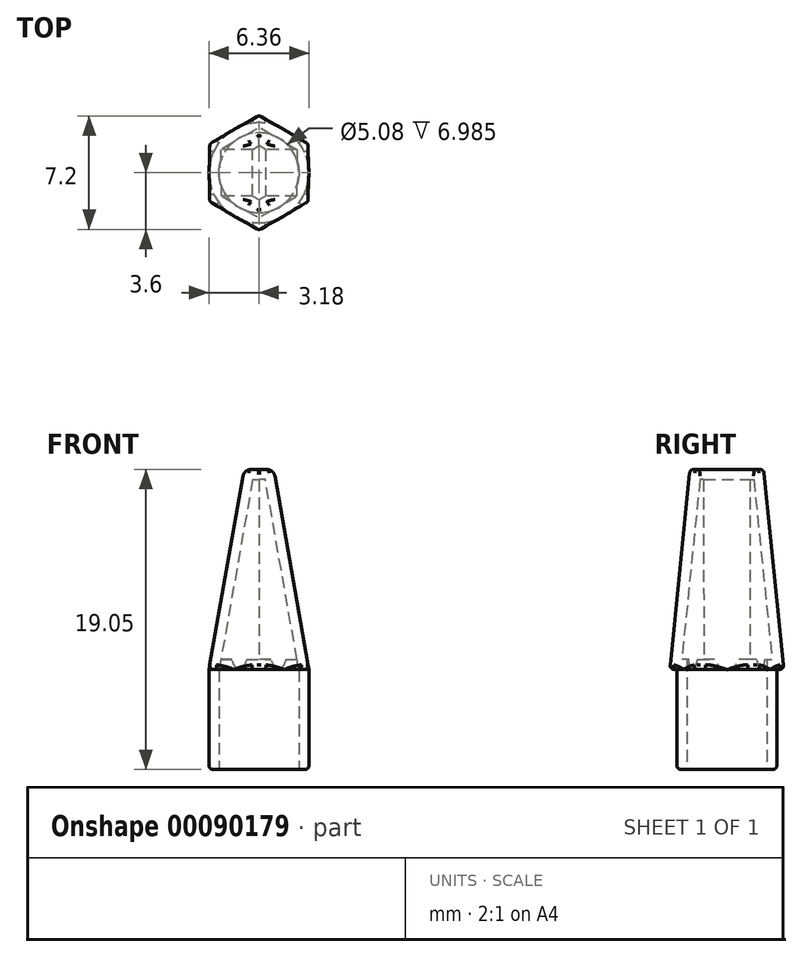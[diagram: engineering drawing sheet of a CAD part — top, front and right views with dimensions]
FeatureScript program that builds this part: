
annotation { "Feature Type Name" : "Feature", "Feature Type Description" : "" }
export const myFeature = defineFeature(function(context is Context, id is Id, definition is map)
    precondition{}
    {
        {
            var Q0;
            Q0=qCreatedBy(makeId("Top.planeOp"),FACE);
            var sketch = newSketch(context, id + "F0", { "sketchPlane" : qUnion([Q0])});
            skCircle(sketch, "E0", {"center": v(0, 0) * mm, "radius": 3.18 * mm});
            skSolve(sketch);
        }
        {
            var Q0;
            Q0=makeQuery(id+"F0.imprint","IMPRINT",FACE,{"disambiguationData":[TD([[makeQuery(id+"F0.imprint","IMPRINT",EDGE,{"derivedFrom":sQuery(id+"F0.wireOp",EDGE,"E0")}),1.0]])]});
            extrude(context, id + "F1", {"entities" : qUnion([Q0]), "depth" : 6.35 * mm});
        }
        {
            var Q0;
            Q0=makeQuery(id+"F1.opExtrude","CAP_FACE",FACE,{"disambiguationData":[OSD([sQuery(id+"F0.wireOp",EDGE,"E0")])],"isStart":false});
            var sketch = newSketch(context, id + "F2", { "sketchPlane" : qUnion([Q0])});
            skCircle(sketch, "E1.cCircle", {"center": v(0, 0) * mm, "radius": 3.18 * mm, "construction": true});
            skLineSegment(sketch, "E1.0", {"start": v(-3.18, -1.83) * mm, "end": v(-3.18, 1.83) * mm});
            skLineSegment(sketch, "E1.1", {"start": v(-3.17, 1.83) * mm, "end": v(0, 3.67) * mm});
            skLineSegment(sketch, "E1.2", {"start": v(0, 3.67) * mm, "end": v(3.17, 1.83) * mm});
            skLineSegment(sketch, "E1.3", {"start": v(3.17, 1.83) * mm, "end": v(3.18, -1.83) * mm});
            skLineSegment(sketch, "E1.4", {"start": v(3.18, -1.83) * mm, "end": v(0, -3.67) * mm});
            skLineSegment(sketch, "E1.5", {"start": v(0, -3.67) * mm, "end": v(-3.17, -1.83) * mm});
            skPoint(sketch, "E1.0.midPoint", {"position": v(-3.18, 0) * mm});
            skSolve(sketch);
        }
        {
            var Q0;
            {var subQ0=sQuery(id+"F2.wireOp",EDGE,"E1.5");var subQ1=sQuery(id+"F2.wireOp",EDGE,"E1.0");var subQ2=makeQuery(id+"F2.imprint","INTERSECT",VERTEX,{"derivedFrom":[subQ1,subQ0]});Q0=makeQuery(id+"F2.imprint","IMPRINT",FACE,{"disambiguationData":[TD([[makeQuery(id+"F2.imprint","IMPRINT",EDGE,{"disambiguationData":[TD([[subQ2,-1.0]])],"derivedFrom":subQ1}),-1.0]])]});}
            var Q1;
            {var subQ0=sQuery(id+"F2.wireOp",EDGE,"E1.2");var subQ1=sQuery(id+"F2.wireOp",EDGE,"E1.1");var subQ2=makeQuery(id+"F2.imprint","INTERSECT",VERTEX,{"derivedFrom":[subQ1,subQ0]});Q1=makeQuery(id+"F2.imprint","IMPRINT",FACE,{"disambiguationData":[TD([[makeQuery(id+"F2.imprint","IMPRINT",EDGE,{"disambiguationData":[TD([[subQ2,1.0]])],"derivedFrom":subQ1}),-1.0]])]});}
            var Q2;
            {var subQ0=sQuery(id+"F2.wireOp",EDGE,"E1.3");var subQ1=sQuery(id+"F2.wireOp",EDGE,"E1.2");var subQ2=makeQuery(id+"F2.imprint","INTERSECT",VERTEX,{"derivedFrom":[subQ1,subQ0]});Q2=makeQuery(id+"F2.imprint","IMPRINT",FACE,{"disambiguationData":[TD([[makeQuery(id+"F2.imprint","IMPRINT",EDGE,{"disambiguationData":[TD([[subQ2,1.0]])],"derivedFrom":subQ1}),-1.0]])]});}
            var Q3;
            {var subQ0=sQuery(id+"F2.wireOp",EDGE,"E1.4");var subQ1=sQuery(id+"F2.wireOp",EDGE,"E1.3");var subQ2=makeQuery(id+"F2.imprint","INTERSECT",VERTEX,{"derivedFrom":[subQ1,subQ0]});Q3=makeQuery(id+"F2.imprint","IMPRINT",FACE,{"disambiguationData":[TD([[makeQuery(id+"F2.imprint","IMPRINT",EDGE,{"disambiguationData":[TD([[subQ2,1.0]])],"derivedFrom":subQ1}),-1.0]])]});}
            var Q4;
            {var subQ0=sQuery(id+"F2.wireOp",EDGE,"E1.5");var subQ1=sQuery(id+"F2.wireOp",EDGE,"E1.4");var subQ2=makeQuery(id+"F2.imprint","INTERSECT",VERTEX,{"derivedFrom":[subQ1,subQ0]});Q4=makeQuery(id+"F2.imprint","IMPRINT",FACE,{"disambiguationData":[TD([[makeQuery(id+"F2.imprint","IMPRINT",EDGE,{"disambiguationData":[TD([[subQ2,1.0]])],"derivedFrom":subQ1}),-1.0]])]});}
            var Q5;
            {var subQ0=makeQuery(id+"F1.opExtrude","CAP_EDGE",EDGE,{"disambiguationData":[OSD([sQuery(id+"F0.wireOp",EDGE,"E0")])],"isStart":false});var subQ6=makeQuery(id+"F2.imprint","INTERSECT",VERTEX,{"derivedFrom":[subQ0,sQuery(id+"F2.wireOp",EDGE,"E1.0")]});Q5=makeQuery(id+"F2.imprint","IMPRINT",FACE,{"disambiguationData":[TD([[makeQuery(id+"F2.imprint","IMPRINT",EDGE,{"disambiguationData":[TD([[subQ6,1.0]])],"derivedFrom":subQ0}),1.0]])]});}
            var Q6;
            {var subQ0=sQuery(id+"F2.wireOp",EDGE,"E1.1");var subQ1=sQuery(id+"F2.wireOp",EDGE,"E1.0");var subQ2=makeQuery(id+"F2.imprint","INTERSECT",VERTEX,{"derivedFrom":[subQ1,subQ0]});Q6=makeQuery(id+"F2.imprint","IMPRINT",FACE,{"disambiguationData":[TD([[makeQuery(id+"F2.imprint","IMPRINT",EDGE,{"disambiguationData":[TD([[subQ2,1.0]])],"derivedFrom":subQ1}),-1.0]])]});}
            extrude(context, id + "F3", {"entities" : qUnion([Q0, Q1, Q2, Q3, Q4, Q5, Q6]), "operationType" : NewBodyOperationType.ADD, "depth" : 12.7 * mm});
        }
        {
            var Q0;
            Q0=makeQuery(id+"F3.opExtrude","CAP_EDGE",EDGE,{"disambiguationData":[OSD([sQuery(id+"F2.wireOp",EDGE,"E1.3")])],"isStart":false});
            var Q1;
            Q1=makeQuery(id+"F3.opExtrude","CAP_EDGE",EDGE,{"disambiguationData":[OSD([sQuery(id+"F2.wireOp",EDGE,"E1.0")])],"isStart":false});
            chamfer(context, id + "F4", {"entities" : qUnion([Q0, Q1]), "chamferType" : ChamferType.OFFSET_ANGLE, "width" : 12.7 * mm, "oppositeDirection" : false, "angle" : 10 * degree, "tangentPropagation" : true});
        }
        {
            var Q0;
            Q0=makeQuery(id+"F3.opExtrude","CAP_EDGE",EDGE,{"disambiguationData":[OSD([sQuery(id+"F2.wireOp",EDGE,"E1.2")])],"isStart":false});
            var Q1;
            Q1=makeQuery(id+"F3.opExtrude","CAP_EDGE",EDGE,{"disambiguationData":[OSD([sQuery(id+"F2.wireOp",EDGE,"E1.1")])],"isStart":false});
            var Q2;
            Q2=makeQuery(id+"F3.opExtrude","CAP_EDGE",EDGE,{"disambiguationData":[OSD([sQuery(id+"F2.wireOp",EDGE,"E1.4")])],"isStart":false});
            var Q3;
            Q3=makeQuery(id+"F3.opExtrude","CAP_EDGE",EDGE,{"disambiguationData":[OSD([sQuery(id+"F2.wireOp",EDGE,"E1.5")])],"isStart":false});
            chamfer(context, id + "F5", {"entities" : qUnion([Q0, Q1, Q2, Q3]), "chamferType" : ChamferType.OFFSET_ANGLE, "width" : 12.7 * mm, "oppositeDirection" : false, "angle" : 5 * degree, "tangentPropagation" : true});
        }
        {
            var Q0;
            {var subQ0=sQuery(id+"F2.wireOp",EDGE,"E1.2");Q0=makeQuery(id+"F5.opChamfer","BLEND_EDGE",EDGE,{"blendedFrom":[makeQuery(id+"F3.opExtrude","CAP_EDGE",EDGE,{"disambiguationData":[OSD([subQ0])],"isStart":false}),makeQuery(id+"F3.opExtrude","CAP_FACE",FACE,{"disambiguationData":[OSD([sQuery(id+"F2.wireOp",EDGE,"E1.0"),sQuery(id+"F2.wireOp",EDGE,"E1.1"),subQ0,sQuery(id+"F2.wireOp",EDGE,"E1.3"),sQuery(id+"F2.wireOp",EDGE,"E1.4"),sQuery(id+"F2.wireOp",EDGE,"E1.5")])],"isStart":false})],"blendedInto":[makeQuery(id+"F3.opExtrude","CAP_FACE",FACE,{"disambiguationData":[OSD([sQuery(id+"F2.wireOp",EDGE,"E1.0"),sQuery(id+"F2.wireOp",EDGE,"E1.1"),subQ0,sQuery(id+"F2.wireOp",EDGE,"E1.3"),sQuery(id+"F2.wireOp",EDGE,"E1.4"),sQuery(id+"F2.wireOp",EDGE,"E1.5")])],"isStart":false})]});}
            var Q1;
            {var subQ0=sQuery(id+"F2.wireOp",EDGE,"E1.1");Q1=makeQuery(id+"F5.opChamfer","BLEND_EDGE",EDGE,{"blendedFrom":[makeQuery(id+"F3.opExtrude","CAP_EDGE",EDGE,{"disambiguationData":[OSD([subQ0])],"isStart":false}),makeQuery(id+"F3.opExtrude","CAP_FACE",FACE,{"disambiguationData":[OSD([sQuery(id+"F2.wireOp",EDGE,"E1.0"),subQ0,sQuery(id+"F2.wireOp",EDGE,"E1.2"),sQuery(id+"F2.wireOp",EDGE,"E1.3"),sQuery(id+"F2.wireOp",EDGE,"E1.4"),sQuery(id+"F2.wireOp",EDGE,"E1.5")])],"isStart":false})],"blendedInto":[makeQuery(id+"F3.opExtrude","CAP_FACE",FACE,{"disambiguationData":[OSD([sQuery(id+"F2.wireOp",EDGE,"E1.0"),subQ0,sQuery(id+"F2.wireOp",EDGE,"E1.2"),sQuery(id+"F2.wireOp",EDGE,"E1.3"),sQuery(id+"F2.wireOp",EDGE,"E1.4"),sQuery(id+"F2.wireOp",EDGE,"E1.5")])],"isStart":false})]});}
            var Q2;
            {var subQ0=sQuery(id+"F2.wireOp",EDGE,"E1.5");Q2=makeQuery(id+"F5.opChamfer","BLEND_EDGE",EDGE,{"blendedFrom":[makeQuery(id+"F3.opExtrude","CAP_EDGE",EDGE,{"disambiguationData":[OSD([subQ0])],"isStart":false}),makeQuery(id+"F3.opExtrude","CAP_FACE",FACE,{"disambiguationData":[OSD([sQuery(id+"F2.wireOp",EDGE,"E1.0"),sQuery(id+"F2.wireOp",EDGE,"E1.1"),sQuery(id+"F2.wireOp",EDGE,"E1.2"),sQuery(id+"F2.wireOp",EDGE,"E1.3"),sQuery(id+"F2.wireOp",EDGE,"E1.4"),subQ0])],"isStart":false})],"blendedInto":[makeQuery(id+"F3.opExtrude","CAP_FACE",FACE,{"disambiguationData":[OSD([sQuery(id+"F2.wireOp",EDGE,"E1.0"),sQuery(id+"F2.wireOp",EDGE,"E1.1"),sQuery(id+"F2.wireOp",EDGE,"E1.2"),sQuery(id+"F2.wireOp",EDGE,"E1.3"),sQuery(id+"F2.wireOp",EDGE,"E1.4"),subQ0])],"isStart":false})]});}
            var Q3;
            {var subQ0=sQuery(id+"F2.wireOp",EDGE,"E1.4");Q3=makeQuery(id+"F5.opChamfer","BLEND_EDGE",EDGE,{"blendedFrom":[makeQuery(id+"F3.opExtrude","CAP_EDGE",EDGE,{"disambiguationData":[OSD([subQ0])],"isStart":false}),makeQuery(id+"F3.opExtrude","CAP_FACE",FACE,{"disambiguationData":[OSD([sQuery(id+"F2.wireOp",EDGE,"E1.0"),sQuery(id+"F2.wireOp",EDGE,"E1.1"),sQuery(id+"F2.wireOp",EDGE,"E1.2"),sQuery(id+"F2.wireOp",EDGE,"E1.3"),subQ0,sQuery(id+"F2.wireOp",EDGE,"E1.5")])],"isStart":false})],"blendedInto":[makeQuery(id+"F3.opExtrude","CAP_FACE",FACE,{"disambiguationData":[OSD([sQuery(id+"F2.wireOp",EDGE,"E1.0"),sQuery(id+"F2.wireOp",EDGE,"E1.1"),sQuery(id+"F2.wireOp",EDGE,"E1.2"),sQuery(id+"F2.wireOp",EDGE,"E1.3"),subQ0,sQuery(id+"F2.wireOp",EDGE,"E1.5")])],"isStart":false})]});}
            var Q4;
            Q4=makeQuery(id+"F5.opChamfer","BLEND_EDGE",EDGE,{"blendedFrom":[makeQuery(id+"F3.opExtrude","CAP_EDGE",EDGE,{"disambiguationData":[OSD([sQuery(id+"F2.wireOp",EDGE,"E1.2")])],"isStart":false}),makeQuery(id+"F4.opChamfer","BLEND_FACE",FACE,{"disambiguationData":[OSD([sQuery(id+"F2.wireOp",EDGE,"E1.3")])]})],"blendedInto":[makeQuery(id+"F4.opChamfer","BLEND_FACE",FACE,{"disambiguationData":[OSD([sQuery(id+"F2.wireOp",EDGE,"E1.3")])]})]});
            var Q5;
            Q5=makeQuery(id+"F5.opChamfer","BLEND_EDGE",EDGE,{"blendedFrom":[makeQuery(id+"F3.opExtrude","CAP_EDGE",EDGE,{"disambiguationData":[OSD([sQuery(id+"F2.wireOp",EDGE,"E1.1")])],"isStart":false}),makeQuery(id+"F3.opExtrude","CAP_EDGE",EDGE,{"disambiguationData":[OSD([sQuery(id+"F2.wireOp",EDGE,"E1.2")])],"isStart":false})],"blendedInto":[]});
            var Q6;
            Q6=makeQuery(id+"F5.opChamfer","BLEND_EDGE",EDGE,{"blendedFrom":[makeQuery(id+"F3.opExtrude","CAP_EDGE",EDGE,{"disambiguationData":[OSD([sQuery(id+"F2.wireOp",EDGE,"E1.1")])],"isStart":false}),makeQuery(id+"F4.opChamfer","BLEND_FACE",FACE,{"disambiguationData":[OSD([sQuery(id+"F2.wireOp",EDGE,"E1.0")])]})],"blendedInto":[makeQuery(id+"F4.opChamfer","BLEND_FACE",FACE,{"disambiguationData":[OSD([sQuery(id+"F2.wireOp",EDGE,"E1.0")])]})]});
            var Q7;
            Q7=makeQuery(id+"F5.opChamfer","BLEND_EDGE",EDGE,{"blendedFrom":[makeQuery(id+"F3.opExtrude","CAP_EDGE",EDGE,{"disambiguationData":[OSD([sQuery(id+"F2.wireOp",EDGE,"E1.5")])],"isStart":false}),makeQuery(id+"F4.opChamfer","BLEND_FACE",FACE,{"disambiguationData":[OSD([sQuery(id+"F2.wireOp",EDGE,"E1.0")])]})],"blendedInto":[makeQuery(id+"F4.opChamfer","BLEND_FACE",FACE,{"disambiguationData":[OSD([sQuery(id+"F2.wireOp",EDGE,"E1.0")])]})]});
            var Q8;
            Q8=makeQuery(id+"F5.opChamfer","BLEND_EDGE",EDGE,{"blendedFrom":[makeQuery(id+"F3.opExtrude","CAP_EDGE",EDGE,{"disambiguationData":[OSD([sQuery(id+"F2.wireOp",EDGE,"E1.4")])],"isStart":false}),makeQuery(id+"F3.opExtrude","CAP_EDGE",EDGE,{"disambiguationData":[OSD([sQuery(id+"F2.wireOp",EDGE,"E1.5")])],"isStart":false})],"blendedInto":[]});
            var Q9;
            Q9=makeQuery(id+"F5.opChamfer","BLEND_EDGE",EDGE,{"blendedFrom":[makeQuery(id+"F3.opExtrude","CAP_EDGE",EDGE,{"disambiguationData":[OSD([sQuery(id+"F2.wireOp",EDGE,"E1.4")])],"isStart":false}),makeQuery(id+"F4.opChamfer","BLEND_FACE",FACE,{"disambiguationData":[OSD([sQuery(id+"F2.wireOp",EDGE,"E1.3")])]})],"blendedInto":[makeQuery(id+"F4.opChamfer","BLEND_FACE",FACE,{"disambiguationData":[OSD([sQuery(id+"F2.wireOp",EDGE,"E1.3")])]})]});
            var Q10;
            {var subQ0=sQuery(id+"F2.wireOp",EDGE,"E1.5");var subQ1=sQuery(id+"F2.wireOp",EDGE,"E1.4");var subQ2=makeQuery(id+"F3.opExtrude","CAP_FACE",FACE,{"disambiguationData":[OSD([sQuery(id+"F2.wireOp",EDGE,"E1.0"),sQuery(id+"F2.wireOp",EDGE,"E1.1"),sQuery(id+"F2.wireOp",EDGE,"E1.2"),sQuery(id+"F2.wireOp",EDGE,"E1.3"),subQ1,subQ0])],"isStart":true});Q10=makeQuery(id+"F5.opChamfer","BLEND_EDGE",EDGE,{"blendedFrom":[makeQuery(id+"F3.opExtrude","CAP_EDGE",EDGE,{"disambiguationData":[OSD([subQ0])],"isStart":false}),makeQuery(id+"F3.boolean.opBoolean","SPLIT",FACE,{"disambiguationData":[TD([makeQuery(id+"F1.opExtrude","SWEPT_FACE",FACE,{"disambiguationData":[OSD([sQuery(id+"F0.wireOp",EDGE,"E0")])]}),subQ2,makeQuery(id+"F3.opExtrude","SWEPT_FACE",FACE,{"disambiguationData":[OSD([subQ1])]}),makeQuery(id+"F3.opExtrude","SWEPT_FACE",FACE,{"disambiguationData":[OSD([subQ0])]})])],"derivedFrom":subQ2})],"blendedInto":[makeQuery(id+"F3.boolean.opBoolean","SPLIT",FACE,{"disambiguationData":[TD([makeQuery(id+"F1.opExtrude","SWEPT_FACE",FACE,{"disambiguationData":[OSD([sQuery(id+"F0.wireOp",EDGE,"E0")])]}),subQ2,makeQuery(id+"F3.opExtrude","SWEPT_FACE",FACE,{"disambiguationData":[OSD([subQ1])]}),makeQuery(id+"F3.opExtrude","SWEPT_FACE",FACE,{"disambiguationData":[OSD([subQ0])]})])],"derivedFrom":subQ2})]});}
            var Q11;
            {var subQ0=sQuery(id+"F2.wireOp",EDGE,"E1.0");var subQ1=sQuery(id+"F2.wireOp",EDGE,"E1.5");var subQ2=makeQuery(id+"F3.opExtrude","CAP_FACE",FACE,{"disambiguationData":[OSD([subQ0,sQuery(id+"F2.wireOp",EDGE,"E1.1"),sQuery(id+"F2.wireOp",EDGE,"E1.2"),sQuery(id+"F2.wireOp",EDGE,"E1.3"),sQuery(id+"F2.wireOp",EDGE,"E1.4"),subQ1])],"isStart":true});Q11=makeQuery(id+"F5.opChamfer","BLEND_EDGE",EDGE,{"blendedFrom":[makeQuery(id+"F3.opExtrude","CAP_EDGE",EDGE,{"disambiguationData":[OSD([subQ1])],"isStart":false}),makeQuery(id+"F3.boolean.opBoolean","SPLIT",FACE,{"disambiguationData":[TD([makeQuery(id+"F1.opExtrude","SWEPT_FACE",FACE,{"disambiguationData":[OSD([sQuery(id+"F0.wireOp",EDGE,"E0")])]}),makeQuery(id+"F3.opExtrude","SWEPT_FACE",FACE,{"disambiguationData":[OSD([subQ0])]}),subQ2,makeQuery(id+"F3.opExtrude","SWEPT_FACE",FACE,{"disambiguationData":[OSD([subQ1])]})])],"derivedFrom":subQ2})],"blendedInto":[makeQuery(id+"F3.boolean.opBoolean","SPLIT",FACE,{"disambiguationData":[TD([makeQuery(id+"F1.opExtrude","SWEPT_FACE",FACE,{"disambiguationData":[OSD([sQuery(id+"F0.wireOp",EDGE,"E0")])]}),makeQuery(id+"F3.opExtrude","SWEPT_FACE",FACE,{"disambiguationData":[OSD([subQ0])]}),subQ2,makeQuery(id+"F3.opExtrude","SWEPT_FACE",FACE,{"disambiguationData":[OSD([subQ1])]})])],"derivedFrom":subQ2})]});}
            var Q12;
            {var subQ0=sQuery(id+"F2.wireOp",EDGE,"E1.5");var subQ1=sQuery(id+"F2.wireOp",EDGE,"E1.4");var subQ2=makeQuery(id+"F3.opExtrude","CAP_FACE",FACE,{"disambiguationData":[OSD([sQuery(id+"F2.wireOp",EDGE,"E1.0"),sQuery(id+"F2.wireOp",EDGE,"E1.1"),sQuery(id+"F2.wireOp",EDGE,"E1.2"),sQuery(id+"F2.wireOp",EDGE,"E1.3"),subQ1,subQ0])],"isStart":true});Q12=makeQuery(id+"F5.opChamfer","BLEND_EDGE",EDGE,{"blendedFrom":[makeQuery(id+"F3.opExtrude","CAP_EDGE",EDGE,{"disambiguationData":[OSD([subQ1])],"isStart":false}),makeQuery(id+"F3.boolean.opBoolean","SPLIT",FACE,{"disambiguationData":[TD([makeQuery(id+"F1.opExtrude","SWEPT_FACE",FACE,{"disambiguationData":[OSD([sQuery(id+"F0.wireOp",EDGE,"E0")])]}),subQ2,makeQuery(id+"F3.opExtrude","SWEPT_FACE",FACE,{"disambiguationData":[OSD([subQ1])]}),makeQuery(id+"F3.opExtrude","SWEPT_FACE",FACE,{"disambiguationData":[OSD([subQ0])]})])],"derivedFrom":subQ2})],"blendedInto":[makeQuery(id+"F3.boolean.opBoolean","SPLIT",FACE,{"disambiguationData":[TD([makeQuery(id+"F1.opExtrude","SWEPT_FACE",FACE,{"disambiguationData":[OSD([sQuery(id+"F0.wireOp",EDGE,"E0")])]}),subQ2,makeQuery(id+"F3.opExtrude","SWEPT_FACE",FACE,{"disambiguationData":[OSD([subQ1])]}),makeQuery(id+"F3.opExtrude","SWEPT_FACE",FACE,{"disambiguationData":[OSD([subQ0])]})])],"derivedFrom":subQ2})]});}
            var Q13;
            {var subQ0=sQuery(id+"F2.wireOp",EDGE,"E1.4");var subQ1=sQuery(id+"F2.wireOp",EDGE,"E1.3");var subQ2=makeQuery(id+"F3.opExtrude","CAP_FACE",FACE,{"disambiguationData":[OSD([sQuery(id+"F2.wireOp",EDGE,"E1.0"),sQuery(id+"F2.wireOp",EDGE,"E1.1"),sQuery(id+"F2.wireOp",EDGE,"E1.2"),subQ1,subQ0,sQuery(id+"F2.wireOp",EDGE,"E1.5")])],"isStart":true});Q13=makeQuery(id+"F5.opChamfer","BLEND_EDGE",EDGE,{"blendedFrom":[makeQuery(id+"F3.opExtrude","CAP_EDGE",EDGE,{"disambiguationData":[OSD([subQ0])],"isStart":false}),makeQuery(id+"F3.boolean.opBoolean","SPLIT",FACE,{"disambiguationData":[TD([makeQuery(id+"F1.opExtrude","SWEPT_FACE",FACE,{"disambiguationData":[OSD([sQuery(id+"F0.wireOp",EDGE,"E0")])]}),subQ2,makeQuery(id+"F3.opExtrude","SWEPT_FACE",FACE,{"disambiguationData":[OSD([subQ1])]}),makeQuery(id+"F3.opExtrude","SWEPT_FACE",FACE,{"disambiguationData":[OSD([subQ0])]})])],"derivedFrom":subQ2})],"blendedInto":[makeQuery(id+"F3.boolean.opBoolean","SPLIT",FACE,{"disambiguationData":[TD([makeQuery(id+"F1.opExtrude","SWEPT_FACE",FACE,{"disambiguationData":[OSD([sQuery(id+"F0.wireOp",EDGE,"E0")])]}),subQ2,makeQuery(id+"F3.opExtrude","SWEPT_FACE",FACE,{"disambiguationData":[OSD([subQ1])]}),makeQuery(id+"F3.opExtrude","SWEPT_FACE",FACE,{"disambiguationData":[OSD([subQ0])]})])],"derivedFrom":subQ2})]});}
            var Q14;
            {var subQ0=sQuery(id+"F2.wireOp",EDGE,"E1.0");var subQ1=sQuery(id+"F2.wireOp",EDGE,"E1.1");var subQ2=makeQuery(id+"F3.opExtrude","CAP_FACE",FACE,{"disambiguationData":[OSD([subQ0,subQ1,sQuery(id+"F2.wireOp",EDGE,"E1.2"),sQuery(id+"F2.wireOp",EDGE,"E1.3"),sQuery(id+"F2.wireOp",EDGE,"E1.4"),sQuery(id+"F2.wireOp",EDGE,"E1.5")])],"isStart":true});Q14=makeQuery(id+"F4.opChamfer","BLEND_EDGE",EDGE,{"blendedFrom":[makeQuery(id+"F3.opExtrude","CAP_EDGE",EDGE,{"disambiguationData":[OSD([subQ0])],"isStart":false}),makeQuery(id+"F3.boolean.opBoolean","SPLIT",FACE,{"disambiguationData":[TD([makeQuery(id+"F1.opExtrude","SWEPT_FACE",FACE,{"disambiguationData":[OSD([sQuery(id+"F0.wireOp",EDGE,"E0")])]}),makeQuery(id+"F3.opExtrude","SWEPT_FACE",FACE,{"disambiguationData":[OSD([subQ0])]}),subQ2,makeQuery(id+"F3.opExtrude","SWEPT_FACE",FACE,{"disambiguationData":[OSD([subQ1])]})])],"derivedFrom":subQ2})],"blendedInto":[makeQuery(id+"F3.boolean.opBoolean","SPLIT",FACE,{"disambiguationData":[TD([makeQuery(id+"F1.opExtrude","SWEPT_FACE",FACE,{"disambiguationData":[OSD([sQuery(id+"F0.wireOp",EDGE,"E0")])]}),makeQuery(id+"F3.opExtrude","SWEPT_FACE",FACE,{"disambiguationData":[OSD([subQ0])]}),subQ2,makeQuery(id+"F3.opExtrude","SWEPT_FACE",FACE,{"disambiguationData":[OSD([subQ1])]})])],"derivedFrom":subQ2})]});}
            var Q15;
            {var subQ0=sQuery(id+"F2.wireOp",EDGE,"E1.0");var subQ1=sQuery(id+"F2.wireOp",EDGE,"E1.1");var subQ2=makeQuery(id+"F3.opExtrude","CAP_FACE",FACE,{"disambiguationData":[OSD([subQ0,subQ1,sQuery(id+"F2.wireOp",EDGE,"E1.2"),sQuery(id+"F2.wireOp",EDGE,"E1.3"),sQuery(id+"F2.wireOp",EDGE,"E1.4"),sQuery(id+"F2.wireOp",EDGE,"E1.5")])],"isStart":true});Q15=makeQuery(id+"F5.opChamfer","BLEND_EDGE",EDGE,{"blendedFrom":[makeQuery(id+"F3.opExtrude","CAP_EDGE",EDGE,{"disambiguationData":[OSD([subQ1])],"isStart":false}),makeQuery(id+"F3.boolean.opBoolean","SPLIT",FACE,{"disambiguationData":[TD([makeQuery(id+"F1.opExtrude","SWEPT_FACE",FACE,{"disambiguationData":[OSD([sQuery(id+"F0.wireOp",EDGE,"E0")])]}),makeQuery(id+"F3.opExtrude","SWEPT_FACE",FACE,{"disambiguationData":[OSD([subQ0])]}),subQ2,makeQuery(id+"F3.opExtrude","SWEPT_FACE",FACE,{"disambiguationData":[OSD([subQ1])]})])],"derivedFrom":subQ2})],"blendedInto":[makeQuery(id+"F3.boolean.opBoolean","SPLIT",FACE,{"disambiguationData":[TD([makeQuery(id+"F1.opExtrude","SWEPT_FACE",FACE,{"disambiguationData":[OSD([sQuery(id+"F0.wireOp",EDGE,"E0")])]}),makeQuery(id+"F3.opExtrude","SWEPT_FACE",FACE,{"disambiguationData":[OSD([subQ0])]}),subQ2,makeQuery(id+"F3.opExtrude","SWEPT_FACE",FACE,{"disambiguationData":[OSD([subQ1])]})])],"derivedFrom":subQ2})]});}
            var Q16;
            {var subQ0=sQuery(id+"F2.wireOp",EDGE,"E1.2");var subQ1=sQuery(id+"F2.wireOp",EDGE,"E1.1");var subQ2=makeQuery(id+"F3.opExtrude","CAP_FACE",FACE,{"disambiguationData":[OSD([sQuery(id+"F2.wireOp",EDGE,"E1.0"),subQ1,subQ0,sQuery(id+"F2.wireOp",EDGE,"E1.3"),sQuery(id+"F2.wireOp",EDGE,"E1.4"),sQuery(id+"F2.wireOp",EDGE,"E1.5")])],"isStart":true});Q16=makeQuery(id+"F5.opChamfer","BLEND_EDGE",EDGE,{"blendedFrom":[makeQuery(id+"F3.opExtrude","CAP_EDGE",EDGE,{"disambiguationData":[OSD([subQ1])],"isStart":false}),makeQuery(id+"F3.boolean.opBoolean","SPLIT",FACE,{"disambiguationData":[TD([makeQuery(id+"F1.opExtrude","SWEPT_FACE",FACE,{"disambiguationData":[OSD([sQuery(id+"F0.wireOp",EDGE,"E0")])]}),subQ2,makeQuery(id+"F3.opExtrude","SWEPT_FACE",FACE,{"disambiguationData":[OSD([subQ1])]}),makeQuery(id+"F3.opExtrude","SWEPT_FACE",FACE,{"disambiguationData":[OSD([subQ0])]})])],"derivedFrom":subQ2})],"blendedInto":[makeQuery(id+"F3.boolean.opBoolean","SPLIT",FACE,{"disambiguationData":[TD([makeQuery(id+"F1.opExtrude","SWEPT_FACE",FACE,{"disambiguationData":[OSD([sQuery(id+"F0.wireOp",EDGE,"E0")])]}),subQ2,makeQuery(id+"F3.opExtrude","SWEPT_FACE",FACE,{"disambiguationData":[OSD([subQ1])]}),makeQuery(id+"F3.opExtrude","SWEPT_FACE",FACE,{"disambiguationData":[OSD([subQ0])]})])],"derivedFrom":subQ2})]});}
            var Q17;
            {var subQ0=sQuery(id+"F2.wireOp",EDGE,"E1.2");var subQ1=sQuery(id+"F2.wireOp",EDGE,"E1.1");var subQ2=makeQuery(id+"F3.opExtrude","CAP_FACE",FACE,{"disambiguationData":[OSD([sQuery(id+"F2.wireOp",EDGE,"E1.0"),subQ1,subQ0,sQuery(id+"F2.wireOp",EDGE,"E1.3"),sQuery(id+"F2.wireOp",EDGE,"E1.4"),sQuery(id+"F2.wireOp",EDGE,"E1.5")])],"isStart":true});Q17=makeQuery(id+"F5.opChamfer","BLEND_EDGE",EDGE,{"blendedFrom":[makeQuery(id+"F3.opExtrude","CAP_EDGE",EDGE,{"disambiguationData":[OSD([subQ0])],"isStart":false}),makeQuery(id+"F3.boolean.opBoolean","SPLIT",FACE,{"disambiguationData":[TD([makeQuery(id+"F1.opExtrude","SWEPT_FACE",FACE,{"disambiguationData":[OSD([sQuery(id+"F0.wireOp",EDGE,"E0")])]}),subQ2,makeQuery(id+"F3.opExtrude","SWEPT_FACE",FACE,{"disambiguationData":[OSD([subQ1])]}),makeQuery(id+"F3.opExtrude","SWEPT_FACE",FACE,{"disambiguationData":[OSD([subQ0])]})])],"derivedFrom":subQ2})],"blendedInto":[makeQuery(id+"F3.boolean.opBoolean","SPLIT",FACE,{"disambiguationData":[TD([makeQuery(id+"F1.opExtrude","SWEPT_FACE",FACE,{"disambiguationData":[OSD([sQuery(id+"F0.wireOp",EDGE,"E0")])]}),subQ2,makeQuery(id+"F3.opExtrude","SWEPT_FACE",FACE,{"disambiguationData":[OSD([subQ1])]}),makeQuery(id+"F3.opExtrude","SWEPT_FACE",FACE,{"disambiguationData":[OSD([subQ0])]})])],"derivedFrom":subQ2})]});}
            var Q18;
            {var subQ0=sQuery(id+"F2.wireOp",EDGE,"E1.3");var subQ1=sQuery(id+"F2.wireOp",EDGE,"E1.2");var subQ2=makeQuery(id+"F3.opExtrude","CAP_FACE",FACE,{"disambiguationData":[OSD([sQuery(id+"F2.wireOp",EDGE,"E1.0"),sQuery(id+"F2.wireOp",EDGE,"E1.1"),subQ1,subQ0,sQuery(id+"F2.wireOp",EDGE,"E1.4"),sQuery(id+"F2.wireOp",EDGE,"E1.5")])],"isStart":true});Q18=makeQuery(id+"F5.opChamfer","BLEND_EDGE",EDGE,{"blendedFrom":[makeQuery(id+"F3.opExtrude","CAP_EDGE",EDGE,{"disambiguationData":[OSD([subQ1])],"isStart":false}),makeQuery(id+"F3.boolean.opBoolean","SPLIT",FACE,{"disambiguationData":[TD([makeQuery(id+"F1.opExtrude","SWEPT_FACE",FACE,{"disambiguationData":[OSD([sQuery(id+"F0.wireOp",EDGE,"E0")])]}),subQ2,makeQuery(id+"F3.opExtrude","SWEPT_FACE",FACE,{"disambiguationData":[OSD([subQ1])]}),makeQuery(id+"F3.opExtrude","SWEPT_FACE",FACE,{"disambiguationData":[OSD([subQ0])]})])],"derivedFrom":subQ2})],"blendedInto":[makeQuery(id+"F3.boolean.opBoolean","SPLIT",FACE,{"disambiguationData":[TD([makeQuery(id+"F1.opExtrude","SWEPT_FACE",FACE,{"disambiguationData":[OSD([sQuery(id+"F0.wireOp",EDGE,"E0")])]}),subQ2,makeQuery(id+"F3.opExtrude","SWEPT_FACE",FACE,{"disambiguationData":[OSD([subQ1])]}),makeQuery(id+"F3.opExtrude","SWEPT_FACE",FACE,{"disambiguationData":[OSD([subQ0])]})])],"derivedFrom":subQ2})]});}
            var Q19;
            {var subQ0=sQuery(id+"F2.wireOp",EDGE,"E1.3");var subQ1=sQuery(id+"F2.wireOp",EDGE,"E1.2");var subQ2=makeQuery(id+"F3.opExtrude","CAP_FACE",FACE,{"disambiguationData":[OSD([sQuery(id+"F2.wireOp",EDGE,"E1.0"),sQuery(id+"F2.wireOp",EDGE,"E1.1"),subQ1,subQ0,sQuery(id+"F2.wireOp",EDGE,"E1.4"),sQuery(id+"F2.wireOp",EDGE,"E1.5")])],"isStart":true});Q19=makeQuery(id+"F4.opChamfer","BLEND_EDGE",EDGE,{"blendedFrom":[makeQuery(id+"F3.opExtrude","CAP_EDGE",EDGE,{"disambiguationData":[OSD([subQ0])],"isStart":false}),makeQuery(id+"F3.boolean.opBoolean","SPLIT",FACE,{"disambiguationData":[TD([makeQuery(id+"F1.opExtrude","SWEPT_FACE",FACE,{"disambiguationData":[OSD([sQuery(id+"F0.wireOp",EDGE,"E0")])]}),subQ2,makeQuery(id+"F3.opExtrude","SWEPT_FACE",FACE,{"disambiguationData":[OSD([subQ1])]}),makeQuery(id+"F3.opExtrude","SWEPT_FACE",FACE,{"disambiguationData":[OSD([subQ0])]})])],"derivedFrom":subQ2})],"blendedInto":[makeQuery(id+"F3.boolean.opBoolean","SPLIT",FACE,{"disambiguationData":[TD([makeQuery(id+"F1.opExtrude","SWEPT_FACE",FACE,{"disambiguationData":[OSD([sQuery(id+"F0.wireOp",EDGE,"E0")])]}),subQ2,makeQuery(id+"F3.opExtrude","SWEPT_FACE",FACE,{"disambiguationData":[OSD([subQ1])]}),makeQuery(id+"F3.opExtrude","SWEPT_FACE",FACE,{"disambiguationData":[OSD([subQ0])]})])],"derivedFrom":subQ2})]});}
            var Q20;
            Q20=makeQuery(id+"F1.opExtrude","CAP_EDGE",EDGE,{"disambiguationData":[OSD([sQuery(id+"F0.wireOp",EDGE,"E0")])],"isStart":true});
            fillet(context, id + "F6", {"entities" : qUnion([Q0, Q1, Q2, Q3, Q4, Q5, Q6, Q7, Q8, Q9, Q10, Q11, Q12, Q13, Q14, Q15, Q16, Q17, Q18, Q19, Q20]), "radius" : 0.25 * mm, "tangentPropagation" : true, "allowEdgeOverflow" : false});
        }
        {
            var Q0;
            Q0=makeQuery(id+"F1.opExtrude","CAP_FACE",FACE,{"disambiguationData":[OSD([sQuery(id+"F0.wireOp",EDGE,"E0")])],"isStart":true});
            shell(context, id + "F7", {"entities" : qUnion([Q0]), "thickness" : 0.64 * mm});
        }
        {
            var Q0;
            {var subQ0=sQuery(id+"F2.wireOp",EDGE,"E1.0");Q0=makeQuery(id+"F4.opChamfer","BLEND_EDGE",EDGE,{"blendedFrom":[makeQuery(id+"F3.opExtrude","CAP_EDGE",EDGE,{"disambiguationData":[OSD([subQ0])],"isStart":false}),makeQuery(id+"F3.opExtrude","CAP_FACE",FACE,{"disambiguationData":[OSD([subQ0,sQuery(id+"F2.wireOp",EDGE,"E1.1"),sQuery(id+"F2.wireOp",EDGE,"E1.2"),sQuery(id+"F2.wireOp",EDGE,"E1.3"),sQuery(id+"F2.wireOp",EDGE,"E1.4"),sQuery(id+"F2.wireOp",EDGE,"E1.5")])],"isStart":false})],"blendedInto":[makeQuery(id+"F3.opExtrude","CAP_FACE",FACE,{"disambiguationData":[OSD([subQ0,sQuery(id+"F2.wireOp",EDGE,"E1.1"),sQuery(id+"F2.wireOp",EDGE,"E1.2"),sQuery(id+"F2.wireOp",EDGE,"E1.3"),sQuery(id+"F2.wireOp",EDGE,"E1.4"),sQuery(id+"F2.wireOp",EDGE,"E1.5")])],"isStart":false})]});}
            var Q1;
            {var subQ0=sQuery(id+"F2.wireOp",EDGE,"E1.3");Q1=makeQuery(id+"F4.opChamfer","BLEND_EDGE",EDGE,{"blendedFrom":[makeQuery(id+"F3.opExtrude","CAP_EDGE",EDGE,{"disambiguationData":[OSD([subQ0])],"isStart":false}),makeQuery(id+"F3.opExtrude","CAP_FACE",FACE,{"disambiguationData":[OSD([sQuery(id+"F2.wireOp",EDGE,"E1.0"),sQuery(id+"F2.wireOp",EDGE,"E1.1"),sQuery(id+"F2.wireOp",EDGE,"E1.2"),subQ0,sQuery(id+"F2.wireOp",EDGE,"E1.4"),sQuery(id+"F2.wireOp",EDGE,"E1.5")])],"isStart":false})],"blendedInto":[makeQuery(id+"F3.opExtrude","CAP_FACE",FACE,{"disambiguationData":[OSD([sQuery(id+"F2.wireOp",EDGE,"E1.0"),sQuery(id+"F2.wireOp",EDGE,"E1.1"),sQuery(id+"F2.wireOp",EDGE,"E1.2"),subQ0,sQuery(id+"F2.wireOp",EDGE,"E1.4"),sQuery(id+"F2.wireOp",EDGE,"E1.5")])],"isStart":false})]});}
            fillet(context, id + "F8", {"entities" : qUnion([Q0, Q1]), "radius" : 0.5 * mm, "tangentPropagation" : true, "allowEdgeOverflow" : false});
        }
    });
